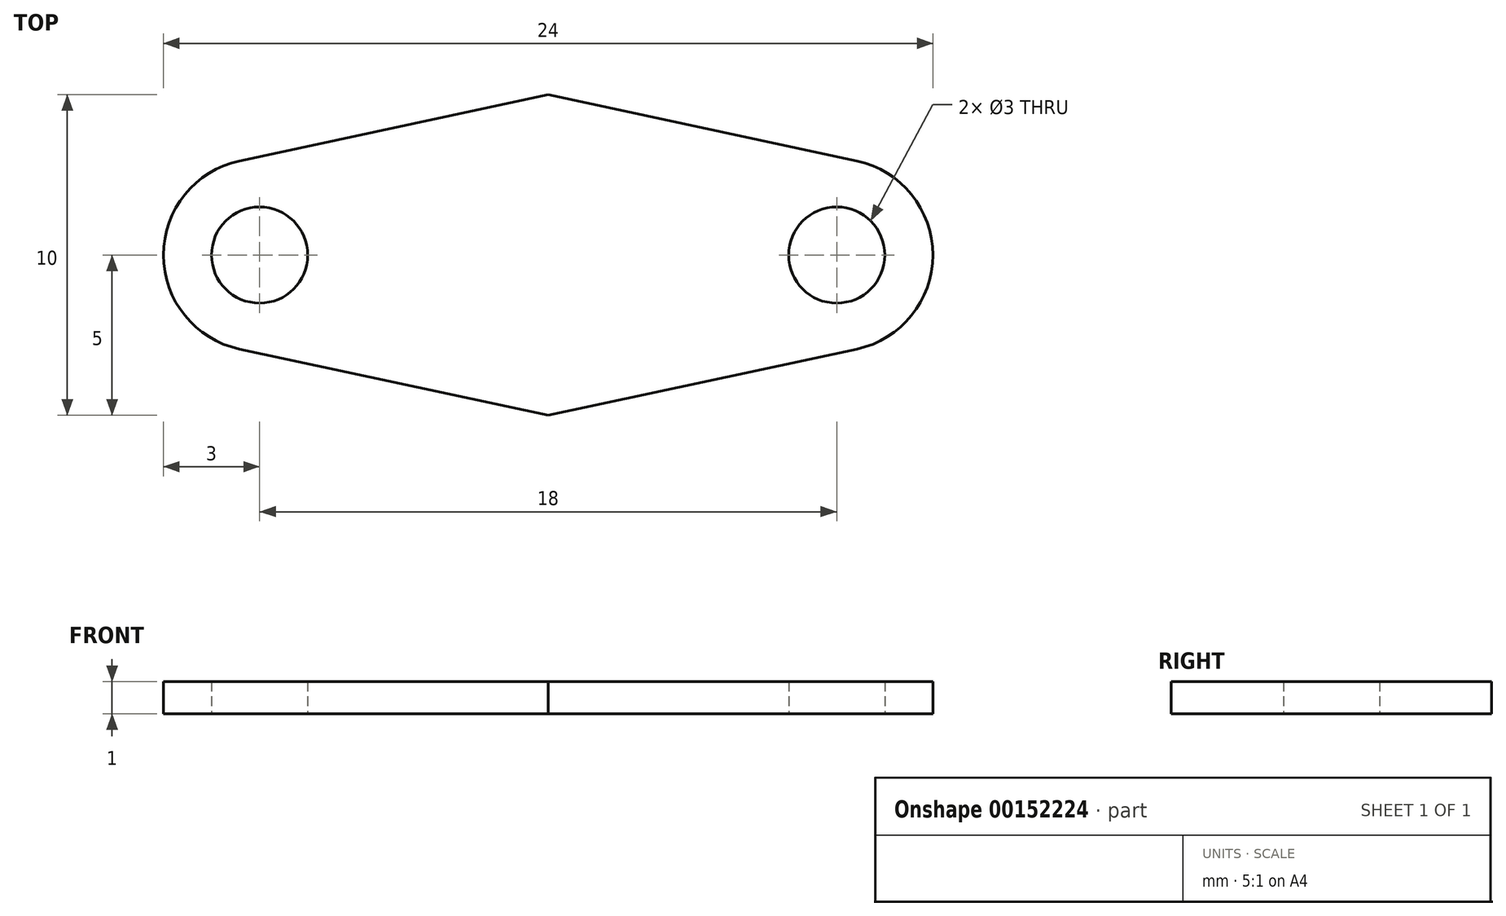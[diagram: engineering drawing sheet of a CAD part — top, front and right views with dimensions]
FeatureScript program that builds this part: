
annotation { "Feature Type Name" : "Feature", "Feature Type Description" : "" }
export const myFeature = defineFeature(function(context is Context, id is Id, definition is map)
    precondition{}
    {
        {
            var Q0;
            Q0=qCreatedBy(makeId("Top.planeOp"),FACE);
            var sketch = newSketch(context, id + "F0", { "sketchPlane" : qUnion([Q0])});
            skLineSegment(sketch, "E0", {"start": v(0, 0) * mm, "end": v(9, 0) * mm});
            skLineSegment(sketch, "E1", {"start": v(0, 0) * mm, "end": v(-9, 0) * mm});
            skCircle(sketch, "E2", {"center": v(-9, 0) * mm, "radius": 1.5 * mm});
            skCircle(sketch, "E3", {"center": v(9, 0) * mm, "radius": 1.5 * mm});
            skCircle(sketch, "E4", {"center": v(9, 0) * mm, "radius": 3 * mm});
            skCircle(sketch, "E5", {"center": v(-9, 0) * mm, "radius": 3 * mm});
            skLineSegment(sketch, "E6", {"start": v(0, 0) * mm, "end": v(0, 5) * mm});
            skLineSegment(sketch, "E7", {"start": v(0, 0) * mm, "end": v(0, -5) * mm});
            skLineSegment(sketch, "E8", {"start": v(0, -5) * mm, "end": v(-9.63, -2.93) * mm});
            skLineSegment(sketch, "E9", {"start": v(0, -5) * mm, "end": v(9.63, -2.93) * mm});
            skLineSegment(sketch, "E10", {"start": v(0, 5) * mm, "end": v(9.63, 2.93) * mm});
            skLineSegment(sketch, "E11", {"start": v(0, 5) * mm, "end": v(-9.63, 2.93) * mm});
            skSolve(sketch);
        }
        {
            var Q0;
            {var subQ0=sQuery(id+"F0.wireOp",EDGE,"E7");Q0=makeQuery(id+"F0.imprint","IMPRINT",FACE,{"disambiguationData":[TD([[makeQuery(id+"F0.imprint","IMPRINT",EDGE,{"derivedFrom":subQ0}),-1.0]])]});}
            var Q1;
            {var subQ0=sQuery(id+"F0.wireOp",EDGE,"E6");Q1=makeQuery(id+"F0.imprint","IMPRINT",FACE,{"disambiguationData":[TD([[makeQuery(id+"F0.imprint","IMPRINT",EDGE,{"derivedFrom":subQ0}),1.0]])]});}
            var Q2;
            {var subQ0=sQuery(id+"F0.wireOp",EDGE,"E6");Q2=makeQuery(id+"F0.imprint","IMPRINT",FACE,{"disambiguationData":[TD([[makeQuery(id+"F0.imprint","IMPRINT",EDGE,{"derivedFrom":subQ0}),-1.0]])]});}
            var Q3;
            {var subQ0=sQuery(id+"F0.wireOp",EDGE,"E7");Q3=makeQuery(id+"F0.imprint","IMPRINT",FACE,{"disambiguationData":[TD([[makeQuery(id+"F0.imprint","IMPRINT",EDGE,{"derivedFrom":subQ0}),1.0]])]});}
            var Q4;
            Q4=makeQuery(id+"F0.imprint","IMPRINT",FACE,{"disambiguationData":[TD([[makeQuery(id+"F0.imprint","IMPRINT",EDGE,{"derivedFrom":sQuery(id+"F0.wireOp",EDGE,"E3")}),-1.0]])]});
            var Q5;
            Q5=makeQuery(id+"F0.imprint","IMPRINT",FACE,{"disambiguationData":[TD([[makeQuery(id+"F0.imprint","IMPRINT",EDGE,{"derivedFrom":sQuery(id+"F0.wireOp",EDGE,"E2")}),-1.0]])]});
            extrude(context, id + "F1", {"entities" : qUnion([Q0, Q1, Q2, Q3, Q4, Q5]), "depth" : 1 * mm});
        }
    });
